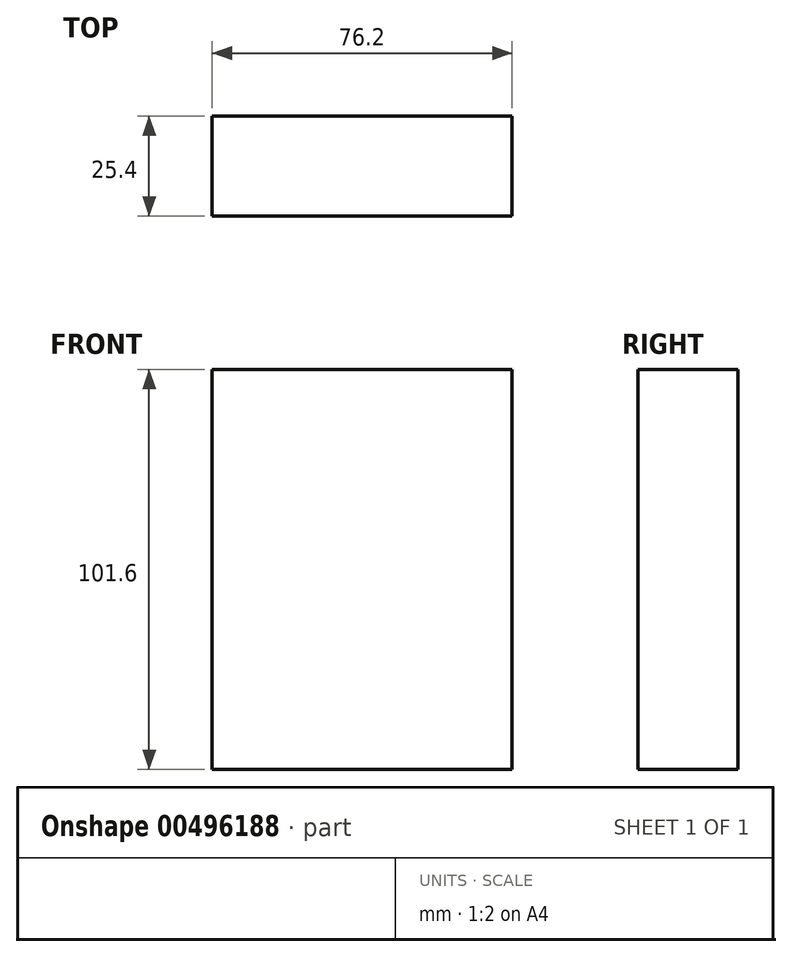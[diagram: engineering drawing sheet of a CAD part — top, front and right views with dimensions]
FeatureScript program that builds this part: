
annotation { "Feature Type Name" : "Feature", "Feature Type Description" : "" }
export const myFeature = defineFeature(function(context is Context, id is Id, definition is map)
    precondition{}
    {
        {
            var Q0;
            Q0=qCreatedBy(makeId("Front.planeOp"),FACE);
            var sketch = newSketch(context, id + "F0", { "sketchPlane" : qUnion([Q0])});
            skLineSegment(sketch, "E0", {"start": v(-18.2, 47.65) * mm, "end": v(-18.2, -53.95) * mm});
            skLineSegment(sketch, "E1", {"start": v(-18.2, -53.95) * mm, "end": v(58, -53.95) * mm});
            skLineSegment(sketch, "E2", {"start": v(58, -53.95) * mm, "end": v(58, 47.65) * mm});
            skLineSegment(sketch, "E3", {"start": v(58, 47.65) * mm, "end": v(-18.2, 47.65) * mm});
            skSolve(sketch);
        }
        {
            var Q0;
            Q0=makeQuery(id+"F0.imprint","IMPRINT",FACE,{"disambiguationData":[TD([[makeQuery(id+"F0.imprint","IMPRINT",EDGE,{"derivedFrom":sQuery(id+"F0.wireOp",EDGE,"E0")}),1.0]])]});
            extrude(context, id + "F1", {"entities" : qUnion([Q0]), "depth" : 25.4 * mm});
        }
    });
